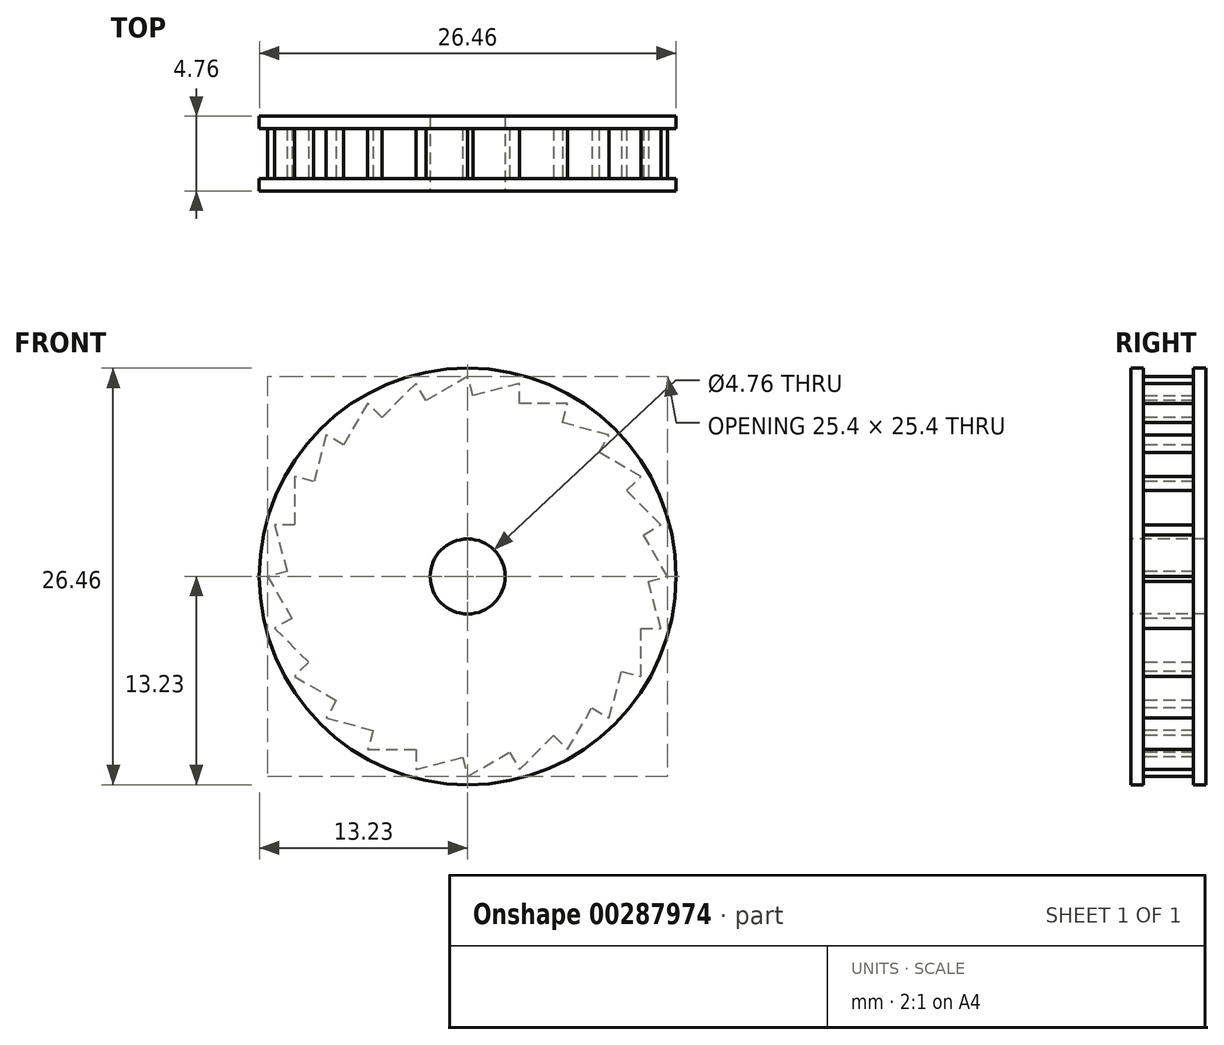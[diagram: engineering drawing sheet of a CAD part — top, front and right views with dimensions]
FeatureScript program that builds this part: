
annotation { "Feature Type Name" : "Feature", "Feature Type Description" : "" }
export const myFeature = defineFeature(function(context is Context, id is Id, definition is map)
    precondition{}
    {
        {
            var Q0;
            Q0=qCreatedBy(makeId("Front.planeOp"),FACE);
            var sketch = newSketch(context, id + "F0", { "sketchPlane" : qUnion([Q0])});
            skLineSegment(sketch, "E0", {"start": v(0, 0) * mm, "end": v(0, 12.7) * mm, "construction": true});
            skLineSegment(sketch, "E1", {"start": v(0, 0) * mm, "end": v(-3.29, 12.27) * mm, "construction": true});
            skLineSegment(sketch, "E2", {"start": v(0, 12.7) * mm, "end": v(-2.65, 11.17) * mm});
            skLineSegment(sketch, "E3", {"start": v(-2.65, 11.17) * mm, "end": v(-3.29, 12.27) * mm});
            skLineSegment(sketch, "E4.1.0", {"start": v(-5.45, 10.1) * mm, "end": v(-6.35, 11) * mm});
            skLineSegment(sketch, "E4.1.1", {"start": v(-3.29, 12.27) * mm, "end": v(-5.45, 10.1) * mm});
            skLineSegment(sketch, "E4.2.0", {"start": v(-7.88, 8.35) * mm, "end": v(-8.98, 8.98) * mm});
            skLineSegment(sketch, "E4.2.1", {"start": v(-6.35, 11) * mm, "end": v(-7.88, 8.35) * mm});
            skLineSegment(sketch, "E4.3.0", {"start": v(-9.77, 6.02) * mm, "end": v(-11, 6.35) * mm});
            skLineSegment(sketch, "E4.3.1", {"start": v(-8.98, 8.98) * mm, "end": v(-9.77, 6.02) * mm});
            skLineSegment(sketch, "E4.4.0", {"start": v(-11, 3.29) * mm, "end": v(-12.27, 3.29) * mm});
            skLineSegment(sketch, "E4.4.1", {"start": v(-11, 6.35) * mm, "end": v(-11, 3.29) * mm});
            skLineSegment(sketch, "E4.5.0", {"start": v(-11.47, 0.33) * mm, "end": v(-12.7, 0) * mm});
            skLineSegment(sketch, "E4.5.1", {"start": v(-12.27, 3.29) * mm, "end": v(-11.47, 0.33) * mm});
            skLineSegment(sketch, "E4.6.0", {"start": v(-11.17, -2.65) * mm, "end": v(-12.27, -3.29) * mm});
            skLineSegment(sketch, "E4.6.1", {"start": v(-12.7, 0) * mm, "end": v(-11.17, -2.65) * mm});
            skLineSegment(sketch, "E4.7.0", {"start": v(-10.1, -5.45) * mm, "end": v(-11, -6.35) * mm});
            skLineSegment(sketch, "E4.7.1", {"start": v(-12.27, -3.29) * mm, "end": v(-10.1, -5.45) * mm});
            skLineSegment(sketch, "E4.8.0", {"start": v(-8.35, -7.88) * mm, "end": v(-8.98, -8.98) * mm});
            skLineSegment(sketch, "E4.8.1", {"start": v(-11, -6.35) * mm, "end": v(-8.35, -7.88) * mm});
            skLineSegment(sketch, "E4.9.0", {"start": v(-6.02, -9.77) * mm, "end": v(-6.35, -11) * mm});
            skLineSegment(sketch, "E4.9.1", {"start": v(-8.98, -8.98) * mm, "end": v(-6.02, -9.77) * mm});
            skLineSegment(sketch, "E4.10.0", {"start": v(-3.29, -11) * mm, "end": v(-3.29, -12.27) * mm});
            skLineSegment(sketch, "E4.10.1", {"start": v(-6.35, -11) * mm, "end": v(-3.29, -11) * mm});
            skLineSegment(sketch, "E4.11.0", {"start": v(-0.33, -11.47) * mm, "end": v(0, -12.7) * mm});
            skLineSegment(sketch, "E4.11.1", {"start": v(-3.29, -12.27) * mm, "end": v(-0.33, -11.47) * mm});
            skLineSegment(sketch, "E4.12.0", {"start": v(2.65, -11.17) * mm, "end": v(3.29, -12.27) * mm});
            skLineSegment(sketch, "E4.12.1", {"start": v(0, -12.7) * mm, "end": v(2.65, -11.17) * mm});
            skLineSegment(sketch, "E4.13.0", {"start": v(5.45, -10.1) * mm, "end": v(6.35, -11) * mm});
            skLineSegment(sketch, "E4.13.1", {"start": v(3.29, -12.27) * mm, "end": v(5.45, -10.1) * mm});
            skLineSegment(sketch, "E4.14.0", {"start": v(7.88, -8.35) * mm, "end": v(8.98, -8.98) * mm});
            skLineSegment(sketch, "E4.14.1", {"start": v(6.35, -11) * mm, "end": v(7.88, -8.35) * mm});
            skLineSegment(sketch, "E4.15.0", {"start": v(9.77, -6.02) * mm, "end": v(11, -6.35) * mm});
            skLineSegment(sketch, "E4.15.1", {"start": v(8.98, -8.98) * mm, "end": v(9.77, -6.02) * mm});
            skLineSegment(sketch, "E4.16.0", {"start": v(11, -3.29) * mm, "end": v(12.27, -3.29) * mm});
            skLineSegment(sketch, "E4.16.1", {"start": v(11, -6.35) * mm, "end": v(11, -3.29) * mm});
            skLineSegment(sketch, "E4.17.0", {"start": v(11.47, -0.33) * mm, "end": v(12.7, 0) * mm});
            skLineSegment(sketch, "E4.17.1", {"start": v(12.27, -3.29) * mm, "end": v(11.47, -0.33) * mm});
            skLineSegment(sketch, "E4.18.0", {"start": v(11.17, 2.65) * mm, "end": v(12.27, 3.29) * mm});
            skLineSegment(sketch, "E4.18.1", {"start": v(12.7, 0) * mm, "end": v(11.17, 2.65) * mm});
            skLineSegment(sketch, "E4.19.0", {"start": v(10.1, 5.45) * mm, "end": v(11, 6.35) * mm});
            skLineSegment(sketch, "E4.19.1", {"start": v(12.27, 3.29) * mm, "end": v(10.1, 5.45) * mm});
            skLineSegment(sketch, "E4.20.0", {"start": v(8.35, 7.88) * mm, "end": v(8.98, 8.98) * mm});
            skLineSegment(sketch, "E4.20.1", {"start": v(11, 6.35) * mm, "end": v(8.35, 7.88) * mm});
            skLineSegment(sketch, "E4.21.0", {"start": v(6.02, 9.77) * mm, "end": v(6.35, 11) * mm});
            skLineSegment(sketch, "E4.21.1", {"start": v(8.98, 8.98) * mm, "end": v(6.02, 9.77) * mm});
            skLineSegment(sketch, "E4.22.0", {"start": v(3.29, 11) * mm, "end": v(3.29, 12.27) * mm});
            skLineSegment(sketch, "E4.22.1", {"start": v(6.35, 11) * mm, "end": v(3.29, 11) * mm});
            skPoint(sketch, "E4.center", {"position": v(0, 0) * mm});
            skLineSegment(sketch, "E5.3.23.0", {"start": v(3.29, 12.27) * mm, "end": v(0.33, 11.47) * mm});
            skLineSegment(sketch, "E5.4.23.0", {"start": v(0.33, 11.47) * mm, "end": v(0, 12.7) * mm});
            skSolve(sketch);
        }
        {
            var Q0;
            Q0 = qSketchRegion(id + "F0", true);
            extrude(context, id + "F1", {"entities" : qUnion([Q0]), "oppositeDirection" : true, "depth" : 3.17 * mm});
        }
        {
            var Q0;
            Q0=makeQuery(id+"F1.opExtrude","CAP_FACE",FACE,{"disambiguationData":[OSD([sQuery(id+"F0.wireOp",EDGE,"E4.1.0"),sQuery(id+"F0.wireOp",EDGE,"E4.1.1"),sQuery(id+"F0.wireOp",EDGE,"E4.2.0"),sQuery(id+"F0.wireOp",EDGE,"E4.2.1"),sQuery(id+"F0.wireOp",EDGE,"E4.3.0"),sQuery(id+"F0.wireOp",EDGE,"E4.3.1"),sQuery(id+"F0.wireOp",EDGE,"E4.4.0"),sQuery(id+"F0.wireOp",EDGE,"E4.4.1"),sQuery(id+"F0.wireOp",EDGE,"E4.5.0"),sQuery(id+"F0.wireOp",EDGE,"E4.5.1"),sQuery(id+"F0.wireOp",EDGE,"E4.6.0"),sQuery(id+"F0.wireOp",EDGE,"E4.6.1"),sQuery(id+"F0.wireOp",EDGE,"E4.7.0"),sQuery(id+"F0.wireOp",EDGE,"E4.7.1"),sQuery(id+"F0.wireOp",EDGE,"E4.8.0"),sQuery(id+"F0.wireOp",EDGE,"E4.8.1"),sQuery(id+"F0.wireOp",EDGE,"E4.9.0"),sQuery(id+"F0.wireOp",EDGE,"E4.9.1"),sQuery(id+"F0.wireOp",EDGE,"E4.10.0"),sQuery(id+"F0.wireOp",EDGE,"E4.10.1"),sQuery(id+"F0.wireOp",EDGE,"E4.11.0"),sQuery(id+"F0.wireOp",EDGE,"E4.11.1"),sQuery(id+"F0.wireOp",EDGE,"E4.12.0"),sQuery(id+"F0.wireOp",EDGE,"E4.12.1"),sQuery(id+"F0.wireOp",EDGE,"E4.13.0"),sQuery(id+"F0.wireOp",EDGE,"E4.13.1"),sQuery(id+"F0.wireOp",EDGE,"E4.14.0"),sQuery(id+"F0.wireOp",EDGE,"E4.14.1"),sQuery(id+"F0.wireOp",EDGE,"E4.15.0"),sQuery(id+"F0.wireOp",EDGE,"E4.15.1"),sQuery(id+"F0.wireOp",EDGE,"E4.16.0"),sQuery(id+"F0.wireOp",EDGE,"E4.16.1"),sQuery(id+"F0.wireOp",EDGE,"E4.17.0"),sQuery(id+"F0.wireOp",EDGE,"E4.17.1"),sQuery(id+"F0.wireOp",EDGE,"E4.18.0"),sQuery(id+"F0.wireOp",EDGE,"E4.18.1"),sQuery(id+"F0.wireOp",EDGE,"E4.19.0"),sQuery(id+"F0.wireOp",EDGE,"E4.19.1"),sQuery(id+"F0.wireOp",EDGE,"E4.20.0"),sQuery(id+"F0.wireOp",EDGE,"E4.20.1"),sQuery(id+"F0.wireOp",EDGE,"E4.21.0"),sQuery(id+"F0.wireOp",EDGE,"E4.21.1"),sQuery(id+"F0.wireOp",EDGE,"E4.22.0"),sQuery(id+"F0.wireOp",EDGE,"E4.22.1"),sQuery(id+"F0.wireOp",EDGE,"E5.3.23.0"),sQuery(id+"F0.wireOp",EDGE,"E5.4.23.0"),sQuery(id+"F0.wireOp",EDGE,"E2"),sQuery(id+"F0.wireOp",EDGE,"E3")])],"isStart":true});
            var sketch = newSketch(context, id + "F2", { "sketchPlane" : qUnion([Q0])});
            skCircle(sketch, "E6", {"center": v(0, 0) * mm, "radius": 2.38 * mm});
            skSolve(sketch);
        }
        {
            var Q0;
            Q0 = qSketchRegion(id + "F2", true);
            extrude(context, id + "F3", {"entities" : qUnion([Q0]), "operationType" : NewBodyOperationType.REMOVE, "oppositeDirection" : true, "depth" : 25.4 * mm});
        }
        {
            var Q0;
            Q0=makeQuery(id+"F1.opExtrude","CAP_FACE",FACE,{"disambiguationData":[OSD([sQuery(id+"F0.wireOp",EDGE,"E4.1.0"),sQuery(id+"F0.wireOp",EDGE,"E4.1.1"),sQuery(id+"F0.wireOp",EDGE,"E4.2.0"),sQuery(id+"F0.wireOp",EDGE,"E4.2.1"),sQuery(id+"F0.wireOp",EDGE,"E4.3.0"),sQuery(id+"F0.wireOp",EDGE,"E4.3.1"),sQuery(id+"F0.wireOp",EDGE,"E4.4.0"),sQuery(id+"F0.wireOp",EDGE,"E4.4.1"),sQuery(id+"F0.wireOp",EDGE,"E4.5.0"),sQuery(id+"F0.wireOp",EDGE,"E4.5.1"),sQuery(id+"F0.wireOp",EDGE,"E4.6.0"),sQuery(id+"F0.wireOp",EDGE,"E4.6.1"),sQuery(id+"F0.wireOp",EDGE,"E4.7.0"),sQuery(id+"F0.wireOp",EDGE,"E4.7.1"),sQuery(id+"F0.wireOp",EDGE,"E4.8.0"),sQuery(id+"F0.wireOp",EDGE,"E4.8.1"),sQuery(id+"F0.wireOp",EDGE,"E4.9.0"),sQuery(id+"F0.wireOp",EDGE,"E4.9.1"),sQuery(id+"F0.wireOp",EDGE,"E4.10.0"),sQuery(id+"F0.wireOp",EDGE,"E4.10.1"),sQuery(id+"F0.wireOp",EDGE,"E4.11.0"),sQuery(id+"F0.wireOp",EDGE,"E4.11.1"),sQuery(id+"F0.wireOp",EDGE,"E4.12.0"),sQuery(id+"F0.wireOp",EDGE,"E4.12.1"),sQuery(id+"F0.wireOp",EDGE,"E4.13.0"),sQuery(id+"F0.wireOp",EDGE,"E4.13.1"),sQuery(id+"F0.wireOp",EDGE,"E4.14.0"),sQuery(id+"F0.wireOp",EDGE,"E4.14.1"),sQuery(id+"F0.wireOp",EDGE,"E4.15.0"),sQuery(id+"F0.wireOp",EDGE,"E4.15.1"),sQuery(id+"F0.wireOp",EDGE,"E4.16.0"),sQuery(id+"F0.wireOp",EDGE,"E4.16.1"),sQuery(id+"F0.wireOp",EDGE,"E4.17.0"),sQuery(id+"F0.wireOp",EDGE,"E4.17.1"),sQuery(id+"F0.wireOp",EDGE,"E4.18.0"),sQuery(id+"F0.wireOp",EDGE,"E4.18.1"),sQuery(id+"F0.wireOp",EDGE,"E4.19.0"),sQuery(id+"F0.wireOp",EDGE,"E4.19.1"),sQuery(id+"F0.wireOp",EDGE,"E4.20.0"),sQuery(id+"F0.wireOp",EDGE,"E4.20.1"),sQuery(id+"F0.wireOp",EDGE,"E4.21.0"),sQuery(id+"F0.wireOp",EDGE,"E4.21.1"),sQuery(id+"F0.wireOp",EDGE,"E4.22.0"),sQuery(id+"F0.wireOp",EDGE,"E4.22.1"),sQuery(id+"F0.wireOp",EDGE,"E5.3.23.0"),sQuery(id+"F0.wireOp",EDGE,"E5.4.23.0"),sQuery(id+"F0.wireOp",EDGE,"E2"),sQuery(id+"F0.wireOp",EDGE,"E3")])],"isStart":true});
            var sketch = newSketch(context, id + "F4", { "sketchPlane" : qUnion([Q0])});
            skCircle(sketch, "E7", {"center": v(0, 0) * mm, "radius": 2.38 * mm});
            skCircle(sketch, "E8", {"center": v(0, 0) * mm, "radius": 13.23 * mm});
            skSolve(sketch);
        }
        {
            var Q0;
            Q0 = qSketchRegion(id + "F4", true);
            extrude(context, id + "F5", {"entities" : qUnion([Q0]), "operationType" : NewBodyOperationType.ADD, "depth" : 0.8 * mm});
        }
        {
            var Q0;
            Q0=makeQuery(id+"F1.opExtrude","CAP_FACE",FACE,{"disambiguationData":[OSD([sQuery(id+"F0.wireOp",EDGE,"E4.1.0"),sQuery(id+"F0.wireOp",EDGE,"E4.1.1"),sQuery(id+"F0.wireOp",EDGE,"E4.2.0"),sQuery(id+"F0.wireOp",EDGE,"E4.2.1"),sQuery(id+"F0.wireOp",EDGE,"E4.3.0"),sQuery(id+"F0.wireOp",EDGE,"E4.3.1"),sQuery(id+"F0.wireOp",EDGE,"E4.4.0"),sQuery(id+"F0.wireOp",EDGE,"E4.4.1"),sQuery(id+"F0.wireOp",EDGE,"E4.5.0"),sQuery(id+"F0.wireOp",EDGE,"E4.5.1"),sQuery(id+"F0.wireOp",EDGE,"E4.6.0"),sQuery(id+"F0.wireOp",EDGE,"E4.6.1"),sQuery(id+"F0.wireOp",EDGE,"E4.7.0"),sQuery(id+"F0.wireOp",EDGE,"E4.7.1"),sQuery(id+"F0.wireOp",EDGE,"E4.8.0"),sQuery(id+"F0.wireOp",EDGE,"E4.8.1"),sQuery(id+"F0.wireOp",EDGE,"E4.9.0"),sQuery(id+"F0.wireOp",EDGE,"E4.9.1"),sQuery(id+"F0.wireOp",EDGE,"E4.10.0"),sQuery(id+"F0.wireOp",EDGE,"E4.10.1"),sQuery(id+"F0.wireOp",EDGE,"E4.11.0"),sQuery(id+"F0.wireOp",EDGE,"E4.11.1"),sQuery(id+"F0.wireOp",EDGE,"E4.12.0"),sQuery(id+"F0.wireOp",EDGE,"E4.12.1"),sQuery(id+"F0.wireOp",EDGE,"E4.13.0"),sQuery(id+"F0.wireOp",EDGE,"E4.13.1"),sQuery(id+"F0.wireOp",EDGE,"E4.14.0"),sQuery(id+"F0.wireOp",EDGE,"E4.14.1"),sQuery(id+"F0.wireOp",EDGE,"E4.15.0"),sQuery(id+"F0.wireOp",EDGE,"E4.15.1"),sQuery(id+"F0.wireOp",EDGE,"E4.16.0"),sQuery(id+"F0.wireOp",EDGE,"E4.16.1"),sQuery(id+"F0.wireOp",EDGE,"E4.17.0"),sQuery(id+"F0.wireOp",EDGE,"E4.17.1"),sQuery(id+"F0.wireOp",EDGE,"E4.18.0"),sQuery(id+"F0.wireOp",EDGE,"E4.18.1"),sQuery(id+"F0.wireOp",EDGE,"E4.19.0"),sQuery(id+"F0.wireOp",EDGE,"E4.19.1"),sQuery(id+"F0.wireOp",EDGE,"E4.20.0"),sQuery(id+"F0.wireOp",EDGE,"E4.20.1"),sQuery(id+"F0.wireOp",EDGE,"E4.21.0"),sQuery(id+"F0.wireOp",EDGE,"E4.21.1"),sQuery(id+"F0.wireOp",EDGE,"E4.22.0"),sQuery(id+"F0.wireOp",EDGE,"E4.22.1"),sQuery(id+"F0.wireOp",EDGE,"E5.3.23.0"),sQuery(id+"F0.wireOp",EDGE,"E5.4.23.0"),sQuery(id+"F0.wireOp",EDGE,"E2"),sQuery(id+"F0.wireOp",EDGE,"E3")])],"isStart":false});
            var sketch = newSketch(context, id + "F6", { "sketchPlane" : qUnion([Q0])});
            skCircle(sketch, "E9", {"center": v(0, 0) * mm, "radius": 13.23 * mm});
            skCircle(sketch, "E10", {"center": v(0, 0) * mm, "radius": 2.38 * mm});
            skSolve(sketch);
        }
        {
            var Q0;
            Q0 = qSketchRegion(id + "F6", true);
            extrude(context, id + "F7", {"entities" : qUnion([Q0]), "operationType" : NewBodyOperationType.ADD, "depth" : 0.8 * mm});
        }
    });
